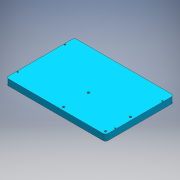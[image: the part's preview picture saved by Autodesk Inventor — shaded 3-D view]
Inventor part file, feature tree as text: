
AUTODESK INVENTOR PART (.ipt)
format: ipt  version: 2016 (Build 200138000, 138)  size: 146,432 bytes
history: native  units: mm
features: sketch x3, hole x2, extrude x1
ambient origin geometry x8: Origin, YZ Plane, XZ Plane, XY Plane, X Axis, Y Axis, Z Axis, Center Point
bodies: Solid1 (feature_tree)
feature tree (6):
  extrude  "baseExtrusion"  Depth=160.0mm
  hole  "baseXYStageMountingHoles"  [1 undecoded]
  hole  "Hole3"  [1 undecoded]
  sketch  "Sketch1"  dims[d0=160.0mm d1=80.0mm]
  sketch  "Sketch2"  dims[d2=110.0mm d3=55.0mm]
  sketch  "Sketch4"  dims[d4=4.0mm d5=10.0mm d6=0.0mm d7=156.6mm d8=78.3mm d9=76.0mm d11=2.013mm d12=5.0mm d13=4.0mm d14=2.0mm d15=90.0deg d16=7.6mm d17=20.594885mm d18=38.0mm d30=40.0mm d31=67.5mm d32=5.0mm d33=5.0mm d34=3.242mm d35=8.0mm d36=4.0mm d37=2.0mm d38=90.0deg d39=11.8mm d40=20.594885mm]
note: 2 required parameter values undecoded (feature->parameter linkage not recoverable at this tier; creation-order binding heuristic only, values carry confidence <= 0.55)
